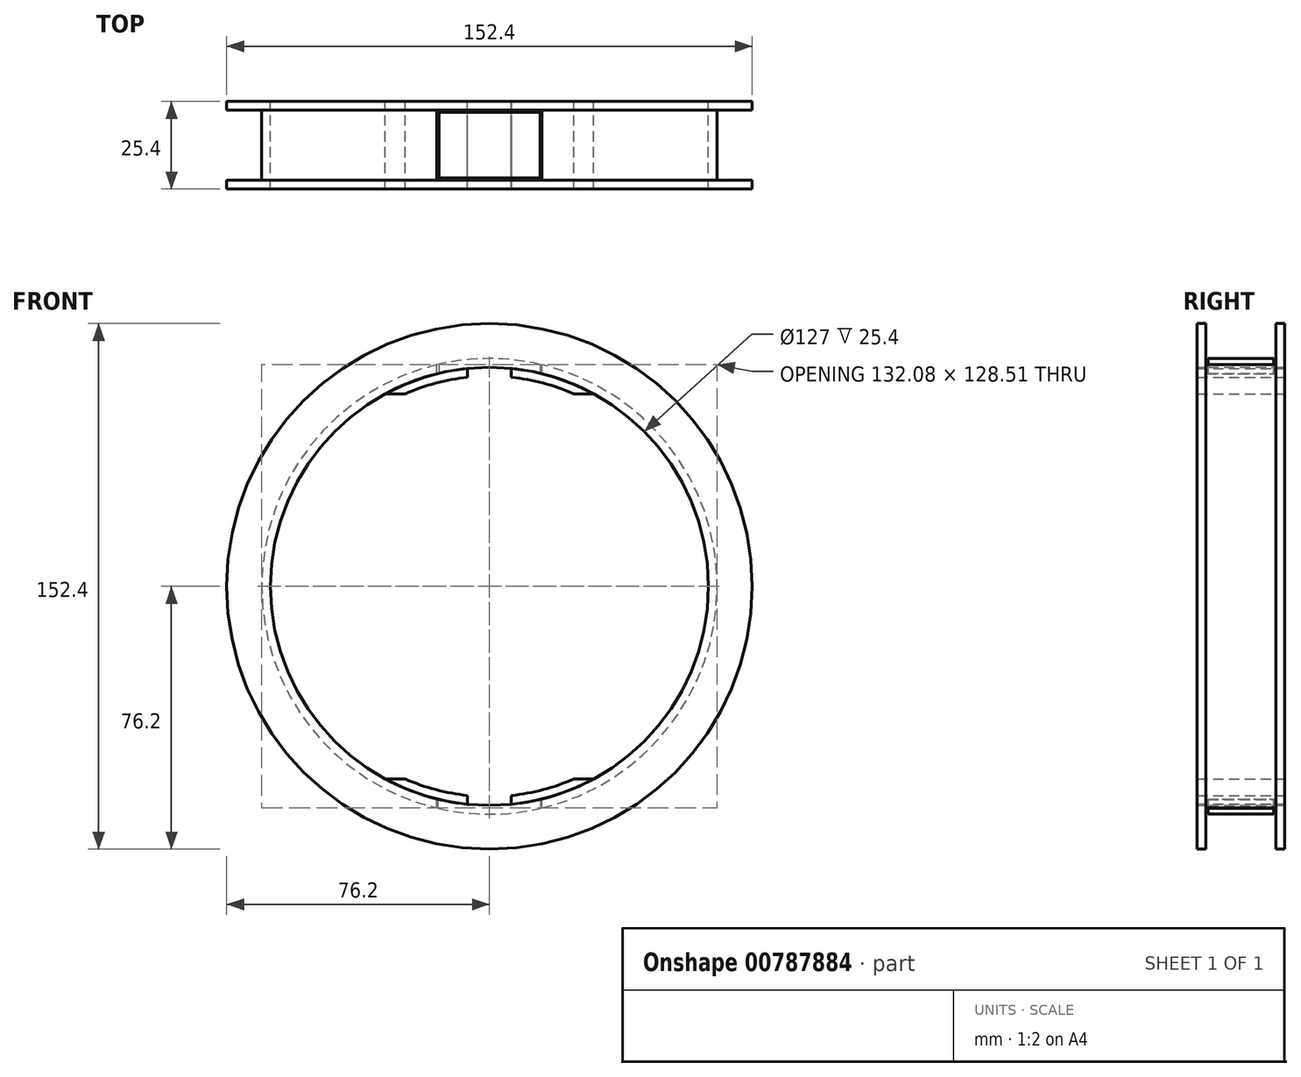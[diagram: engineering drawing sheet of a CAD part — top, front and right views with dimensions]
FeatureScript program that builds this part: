
annotation { "Feature Type Name" : "Feature", "Feature Type Description" : "" }
export const myFeature = defineFeature(function(context is Context, id is Id, definition is map)
    precondition{}
    {
        {
            var Q0;
            Q0=qCreatedBy(makeId("Front.planeOp"),FACE);
            var sketch = newSketch(context, id + "F0", { "sketchPlane" : qUnion([Q0])});
            skCircle(sketch, "E0", {"center": v(0, 0) * mm, "radius": 63.5 * mm});
            skCircle(sketch, "E1", {"center": v(0, 0) * mm, "radius": 76.2 * mm});
            skSolve(sketch);
        }
        {
            var Q0;
            Q0 = qSketchRegion(id + "F0", true);
            extrude(context, id + "F1", {"entities" : qUnion([Q0]), "depth" : 25.4 * mm, "offsetDistance" : 25.4 * mm, "symmetric" : true});
        }
        {
            var Q0;
            Q0=qCreatedBy(makeId("Top.planeOp"),FACE);
            var sketch = newSketch(context, id + "F2", { "sketchPlane" : qUnion([Q0])});
            skLineSegment(sketch, "E2", {"start": v(-15.24, -10.16) * mm, "end": v(-15.24, 10.16) * mm});
            skLineSegment(sketch, "E3", {"start": v(15.24, -10.16) * mm, "end": v(15.24, 10.16) * mm});
            skLineSegment(sketch, "E4", {"start": v(15.24, -10.16) * mm, "end": v(-15.24, -10.16) * mm});
            skLineSegment(sketch, "E5", {"start": v(15.24, 10.16) * mm, "end": v(-15.24, 10.16) * mm});
            skLineSegment(sketch, "E6", {"start": v(0, 39.62) * mm, "end": v(0, -54.89) * mm});
            skLineSegment(sketch, "E7", {"start": v(22.27, 0) * mm, "end": v(-22.66, 0) * mm, "construction": true});
            skPoint(sketch, "E7.startSnap0", {"position": v(-15.24, 0) * mm});
            skSolve(sketch);
        }
        {
            var Q0;
            Q0=makeQuery(id+"F1.opExtrude","SWEPT_FACE",FACE,{"disambiguationData":[OSD([sQuery(id+"F0.wireOp",EDGE,"E1")])]});
            shell(context, id + "F3", {"entities" : qUnion([Q0]), "thickness" : 2.54 * mm});
        }
        {
            var Q0;
            Q0 = qSketchRegion(id + "F2", true);
            extrude(context, id + "F4", {"entities" : qUnion([Q0]), "operationType" : NewBodyOperationType.REMOVE, "oppositeDirection" : true, "depth" : 132.08 * mm, "offsetDistance" : 25.4 * mm, "symmetric" : true});
        }
        {
            var Q0;
            Q0=qCreatedBy(makeId("Front.planeOp"),FACE);
            var sketch = newSketch(context, id + "F5", { "sketchPlane" : qUnion([Q0])});
            skArc(sketch, "E8", {"start": v(14.74, 61.76) * mm, "mid": v(0.03, 63.5) * mm, "end": v(-14.68, 61.78) * mm});
            skArc(sketch, "E9", {"start": v(-14.96, -64.32) * mm, "mid": v(-0.07, -66.04) * mm, "end": v(14.83, -64.35) * mm});
            skLineSegment(sketch, "E10", {"start": v(-14.68, 64.39) * mm, "end": v(-14.68, 61.78) * mm});
            skLineSegment(sketch, "E11", {"start": v(14.74, 64.37) * mm, "end": v(14.74, 61.76) * mm});
            skLineSegment(sketch, "E12", {"start": v(14.83, -61.74) * mm, "end": v(14.83, -64.35) * mm});
            skLineSegment(sketch, "E13", {"start": v(-14.96, -64.32) * mm, "end": v(-14.96, -61.71) * mm});
            skArc(sketch, "E14.trimOffspring", {"start": v(-14.96, -61.71) * mm, "mid": v(-0.07, -63.5) * mm, "end": v(14.83, -61.74) * mm});
            skArc(sketch, "E15.trimOffspring", {"start": v(14.74, 64.37) * mm, "mid": v(0.03, 66.04) * mm, "end": v(-14.68, 64.39) * mm});
            skSolve(sketch);
        }
        {
            var Q0;
            Q0 = qSketchRegion(id + "F5", true);
            extrude(context, id + "F6", {"entities" : qUnion([Q0]), "depth" : 19.05 * mm, "offsetDistance" : 25.4 * mm, "symmetric" : true});
        }
        {
            var Q0;
            Q0=qCreatedBy(makeId("Front.planeOp"),FACE);
            var sketch = newSketch(context, id + "F7", { "sketchPlane" : qUnion([Q0])});
            skArc(sketch, "E16", {"start": v(-24.43, -55.85) * mm, "mid": v(-15.58, -58.94) * mm, "end": v(-6.35, -60.63) * mm});
            skLineSegment(sketch, "E17", {"start": v(-6.35, 60.63) * mm, "end": v(-6.35, 63.17) * mm});
            skLineSegment(sketch, "E18", {"start": v(6.35, 63.17) * mm, "end": v(6.35, 60.63) * mm});
            skLineSegment(sketch, "E19", {"start": v(29.54, 56.4) * mm, "end": v(23.14, 56.4) * mm});
            skLineSegment(sketch, "E20.trimOffspring", {"start": v(-23.14, 56.4) * mm, "end": v(-29.35, 56.4) * mm});
            skLineSegment(sketch, "E21", {"start": v(-6.35, -63.17) * mm, "end": v(-6.35, -60.63) * mm});
            skLineSegment(sketch, "E22", {"start": v(6.35, -63.17) * mm, "end": v(6.35, -60.63) * mm});
            skLineSegment(sketch, "E23", {"start": v(-30.22, -55.85) * mm, "end": v(-24.43, -55.85) * mm});
            skArc(sketch, "E24", {"start": v(-30.22, -55.85) * mm, "mid": v(-18.62, -60.7) * mm, "end": v(-6.29, -63.19) * mm});
            skArc(sketch, "E25.trimOffspring", {"start": v(23.14, 56.4) * mm, "mid": v(14.9, 59.11) * mm, "end": v(6.35, 60.63) * mm});
            skArc(sketch, "E26.trimOffspring", {"start": v(6.35, -60.63) * mm, "mid": v(15.58, -58.94) * mm, "end": v(24.43, -55.85) * mm});
            skArc(sketch, "E27.trimOffspring", {"start": v(-6.35, 60.63) * mm, "mid": v(-14.9, 59.11) * mm, "end": v(-23.14, 56.4) * mm});
            skArc(sketch, "E28.trimOffspring", {"start": v(-6.35, 63.18) * mm, "mid": v(-18.09, 60.87) * mm, "end": v(-29.18, 56.4) * mm});
            skLineSegment(sketch, "E29", {"start": v(24.43, -55.85) * mm, "end": v(30.22, -55.85) * mm});
            skArc(sketch, "E30.trimOffspring", {"start": v(29.18, 56.4) * mm, "mid": v(18.09, 60.87) * mm, "end": v(6.35, 63.18) * mm});
            skArc(sketch, "E31.trimOffspring", {"start": v(6.4, -63.18) * mm, "mid": v(18.67, -60.7) * mm, "end": v(30.22, -55.85) * mm});
            skLineSegment(sketch, "E32.trimOffspring", {"start": v(6.35, -63.13) * mm, "end": v(6.4, -63.18) * mm});
            skLineSegment(sketch, "E33.MirrorCS", {"start": v(-6.35, -63.13) * mm, "end": v(-6.4, -63.18) * mm});
            skArc(sketch, "E34.MirrorCS", {"start": v(-6.35, -60.63) * mm, "mid": v(-15.58, -58.94) * mm, "end": v(-24.43, -55.85) * mm});
            skLineSegment(sketch, "E35.MirrorCS", {"start": v(-24.43, -55.85) * mm, "end": v(-30.22, -55.85) * mm});
            skArc(sketch, "E36.MirrorCS", {"start": v(-6.4, -63.18) * mm, "mid": v(-18.67, -60.7) * mm, "end": v(-30.22, -55.85) * mm});
            skLineSegment(sketch, "E37.MirrorCS", {"start": v(30.22, -55.85) * mm, "end": v(24.43, -55.85) * mm});
            skArc(sketch, "E38.MirrorCS", {"start": v(30.22, -55.85) * mm, "mid": v(18.62, -60.7) * mm, "end": v(6.29, -63.19) * mm});
            skArc(sketch, "E39.MirrorCS", {"start": v(24.43, -55.85) * mm, "mid": v(15.58, -58.94) * mm, "end": v(6.35, -60.63) * mm});
            skLineSegment(sketch, "E40.MirrorCS", {"start": v(6.35, 63.13) * mm, "end": v(6.4, 63.18) * mm});
            skLineSegment(sketch, "E41.MirrorCS", {"start": v(-6.35, 63.13) * mm, "end": v(-6.4, 63.18) * mm});
            skLineSegment(sketch, "E42.MirrorCS", {"start": v(-6.35, 63.17) * mm, "end": v(-6.35, 60.63) * mm});
            skLineSegment(sketch, "E43.MirrorCS", {"start": v(24.43, 55.85) * mm, "end": v(30.22, 55.85) * mm});
            skLineSegment(sketch, "E44.MirrorCS", {"start": v(-24.43, 55.85) * mm, "end": v(-30.22, 55.85) * mm});
            skArc(sketch, "E45.MirrorCS", {"start": v(6.4, 63.18) * mm, "mid": v(18.67, 60.7) * mm, "end": v(30.22, 55.85) * mm});
            skLineSegment(sketch, "E46.MirrorCS", {"start": v(-30.22, 55.85) * mm, "end": v(-24.43, 55.85) * mm});
            skArc(sketch, "E47.MirrorCS", {"start": v(-6.35, 60.63) * mm, "mid": v(-15.58, 58.94) * mm, "end": v(-24.43, 55.85) * mm});
            skArc(sketch, "E48.MirrorCS", {"start": v(-6.4, 63.18) * mm, "mid": v(-18.67, 60.7) * mm, "end": v(-30.22, 55.85) * mm});
            skArc(sketch, "E49.MirrorCS", {"start": v(6.35, 60.63) * mm, "mid": v(15.58, 58.94) * mm, "end": v(24.43, 55.85) * mm});
            skLineSegment(sketch, "E50.MirrorCS", {"start": v(30.22, 55.85) * mm, "end": v(24.43, 55.85) * mm});
            skArc(sketch, "E51.MirrorCS", {"start": v(30.22, 55.85) * mm, "mid": v(18.62, 60.7) * mm, "end": v(6.29, 63.19) * mm});
            skArc(sketch, "E52.MirrorCS", {"start": v(-24.43, 55.85) * mm, "mid": v(-15.58, 58.94) * mm, "end": v(-6.35, 60.63) * mm});
            skArc(sketch, "E53.MirrorCS", {"start": v(24.43, 55.85) * mm, "mid": v(15.58, 58.94) * mm, "end": v(6.35, 60.63) * mm});
            skArc(sketch, "E54.MirrorCS", {"start": v(-30.22, 55.85) * mm, "mid": v(-18.62, 60.7) * mm, "end": v(-6.29, 63.19) * mm});
            skSolve(sketch);
        }
        {
            var Q0;
            Q0 = qSketchRegion(id + "F7", true);
            extrude(context, id + "F8", {"entities" : qUnion([Q0]), "depth" : 25.4 * mm, "offsetDistance" : 25.4 * mm, "symmetric" : true});
        }
    });
